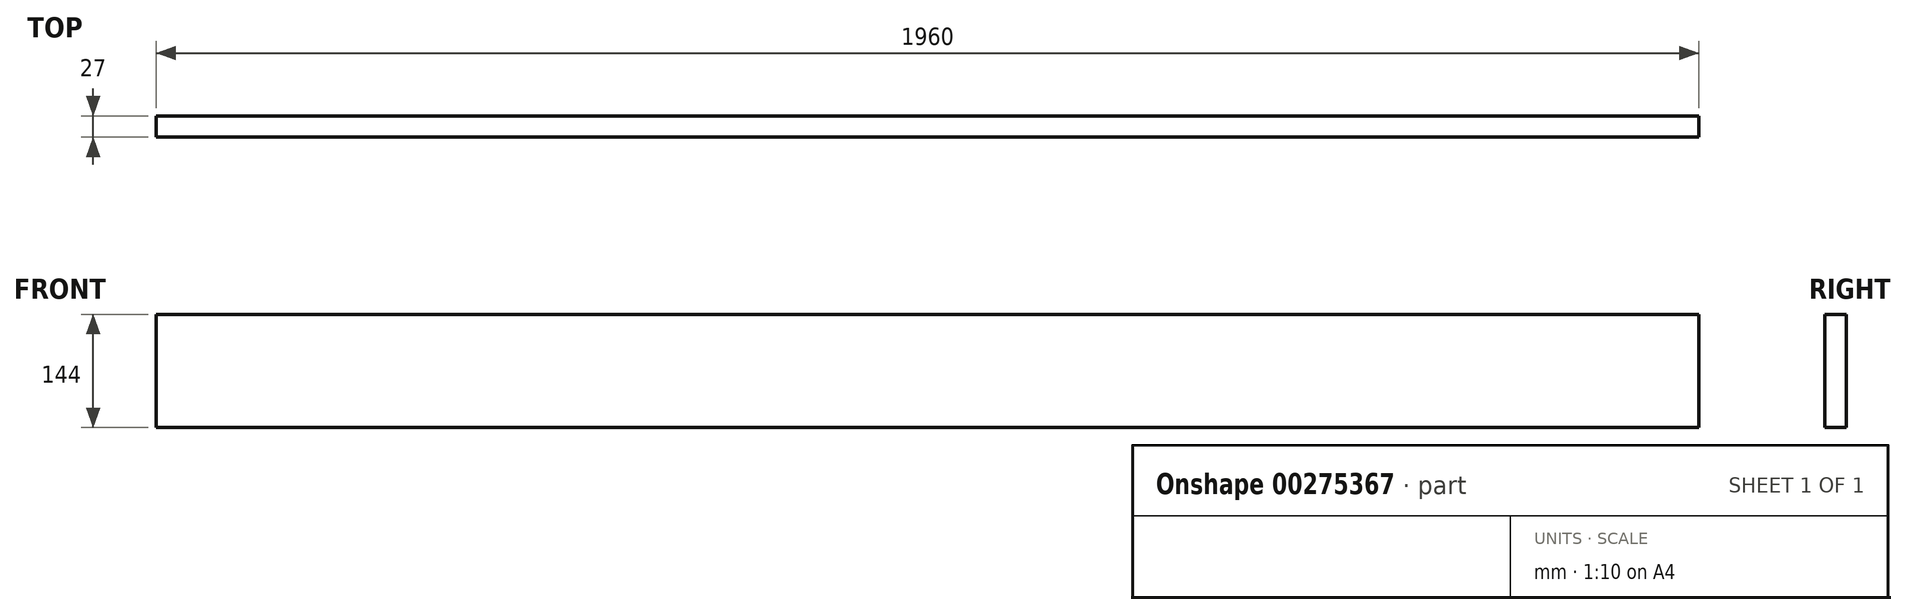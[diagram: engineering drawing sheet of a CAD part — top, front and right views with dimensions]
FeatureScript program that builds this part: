
annotation { "Feature Type Name" : "Feature", "Feature Type Description" : "" }
export const myFeature = defineFeature(function(context is Context, id is Id, definition is map)
    precondition{}
    {
        {
            var Q0;
            Q0=qCreatedBy(makeId("Right.planeOp"),FACE);
            var sketch = newSketch(context, id + "F0", { "sketchPlane" : qUnion([Q0])});
            skLineSegment(sketch, "E0.bottom", {"start": v(-13.5, 72) * mm, "end": v(13.5, 72) * mm});
            skLineSegment(sketch, "E0.top", {"start": v(-13.5, -72) * mm, "end": v(13.5, -72) * mm});
            skLineSegment(sketch, "E0.left", {"start": v(-13.5, 72) * mm, "end": v(-13.5, -72) * mm});
            skLineSegment(sketch, "E0.right", {"start": v(13.5, 72) * mm, "end": v(13.5, -72) * mm});
            skPoint(sketch, "E1", {"position": v(-13.5, 0) * mm});
            skPoint(sketch, "E2", {"position": v(0, 72) * mm});
            skSolve(sketch);
        }
        {
            var Q0;
            Q0=makeQuery(id+"F0.imprint","IMPRINT",FACE,{"disambiguationData":[TD([[makeQuery(id+"F0.imprint","IMPRINT",EDGE,{"derivedFrom":sQuery(id+"F0.wireOp",EDGE,"E0.bottom")}),-1.0]])]});
            extrude(context, id + "F1", {"entities" : qUnion([Q0]), "endBound" : BoundingType.SYMMETRIC, "depth" : (1900 + 30 * 2) * mm});
        }
    });
